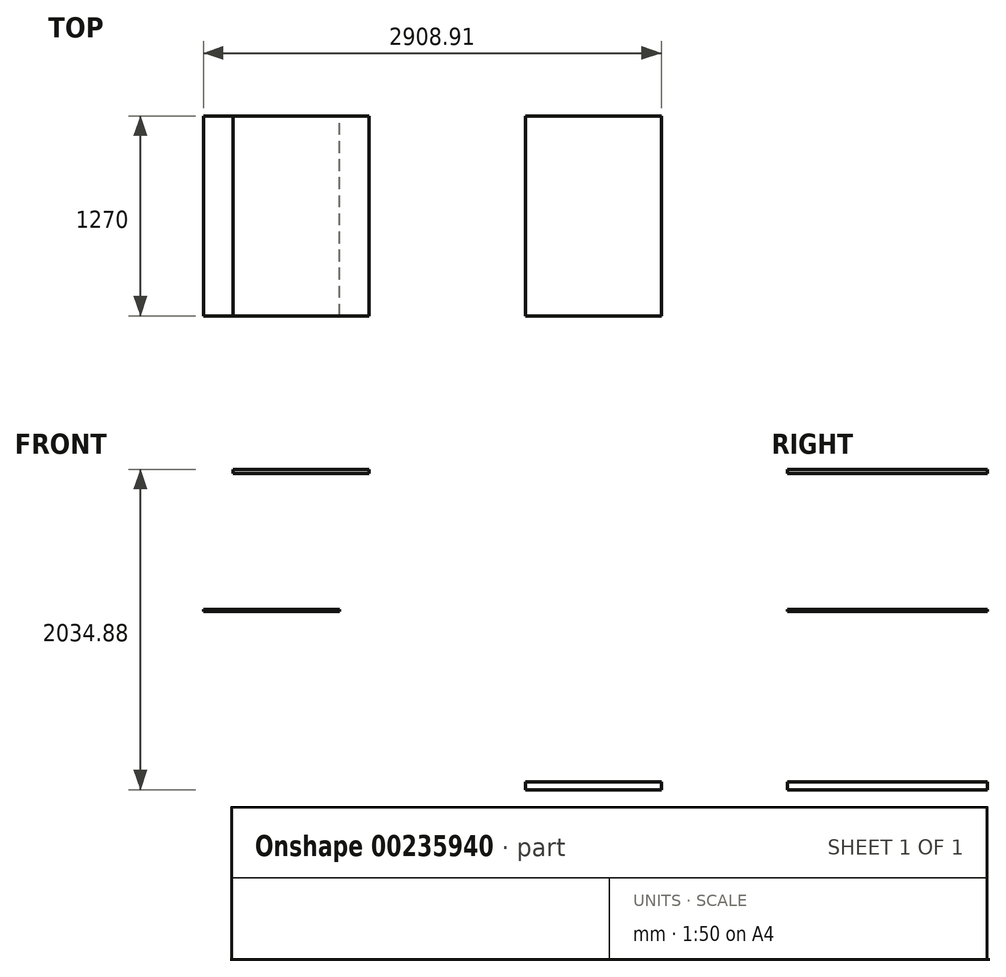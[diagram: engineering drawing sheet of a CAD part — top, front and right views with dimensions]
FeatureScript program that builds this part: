
annotation { "Feature Type Name" : "Feature", "Feature Type Description" : "" }
export const myFeature = defineFeature(function(context is Context, id is Id, definition is map)
    precondition{}
    {
        {
            var Q0;
            Q0=qCreatedBy(makeId("Front.planeOp"),FACE);
            var sketch = newSketch(context, id + "F0", { "sketchPlane" : qUnion([Q0])});
            skLineSegment(sketch, "E0.bottom", {"start": v(-2720.77, 557.9) * mm, "end": v(-1857.17, 557.9) * mm});
            skLineSegment(sketch, "E0.top", {"start": v(-2720.77, 532.5) * mm, "end": v(-1857.17, 532.5) * mm});
            skLineSegment(sketch, "E0.left", {"start": v(-2720.77, 557.9) * mm, "end": v(-2720.77, 532.5) * mm});
            skLineSegment(sketch, "E0.right", {"start": v(-1857.17, 557.9) * mm, "end": v(-1857.17, 532.5) * mm});
            skLineSegment(sketch, "E1.bottom", {"start": v(-2908.91, -331.33) * mm, "end": v(-2045.31, -331.33) * mm});
            skLineSegment(sketch, "E1.top", {"start": v(-2908.91, -344.03) * mm, "end": v(-2045.31, -344.03) * mm});
            skLineSegment(sketch, "E1.left", {"start": v(-2908.91, -331.33) * mm, "end": v(-2908.91, -344.03) * mm});
            skLineSegment(sketch, "E1.right", {"start": v(-2045.31, -331.33) * mm, "end": v(-2045.31, -344.03) * mm});
            skLineSegment(sketch, "E2.bottom", {"start": v(-863.6, -1426.19) * mm, "end": v(0, -1426.19) * mm});
            skLineSegment(sketch, "E2.top", {"start": v(-863.6, -1476.99) * mm, "end": v(0, -1476.99) * mm});
            skLineSegment(sketch, "E2.left", {"start": v(-863.6, -1426.19) * mm, "end": v(-863.6, -1476.99) * mm});
            skLineSegment(sketch, "E2.right", {"start": v(0, -1426.19) * mm, "end": v(0, -1476.99) * mm});
            skSolve(sketch);
        }
        {
            var Q0;
            Q0=makeQuery(id+"F0.imprint","IMPRINT",FACE,{"disambiguationData":[TD([[makeQuery(id+"F0.imprint","IMPRINT",EDGE,{"derivedFrom":sQuery(id+"F0.wireOp",EDGE,"E0.bottom")}),-1.0]])]});
            var Q1;
            Q1=makeQuery(id+"F0.imprint","IMPRINT",FACE,{"disambiguationData":[TD([[makeQuery(id+"F0.imprint","IMPRINT",EDGE,{"derivedFrom":sQuery(id+"F0.wireOp",EDGE,"E2.bottom")}),-1.0]])]});
            var Q2;
            Q2=makeQuery(id+"F0.imprint","IMPRINT",FACE,{"disambiguationData":[TD([[makeQuery(id+"F0.imprint","IMPRINT",EDGE,{"derivedFrom":sQuery(id+"F0.wireOp",EDGE,"E1.bottom")}),-1.0]])]});
            extrude(context, id + "F1", {"entities" : qUnion([Q0, Q1, Q2]), "depth" : 1270 * mm});
        }
    });
